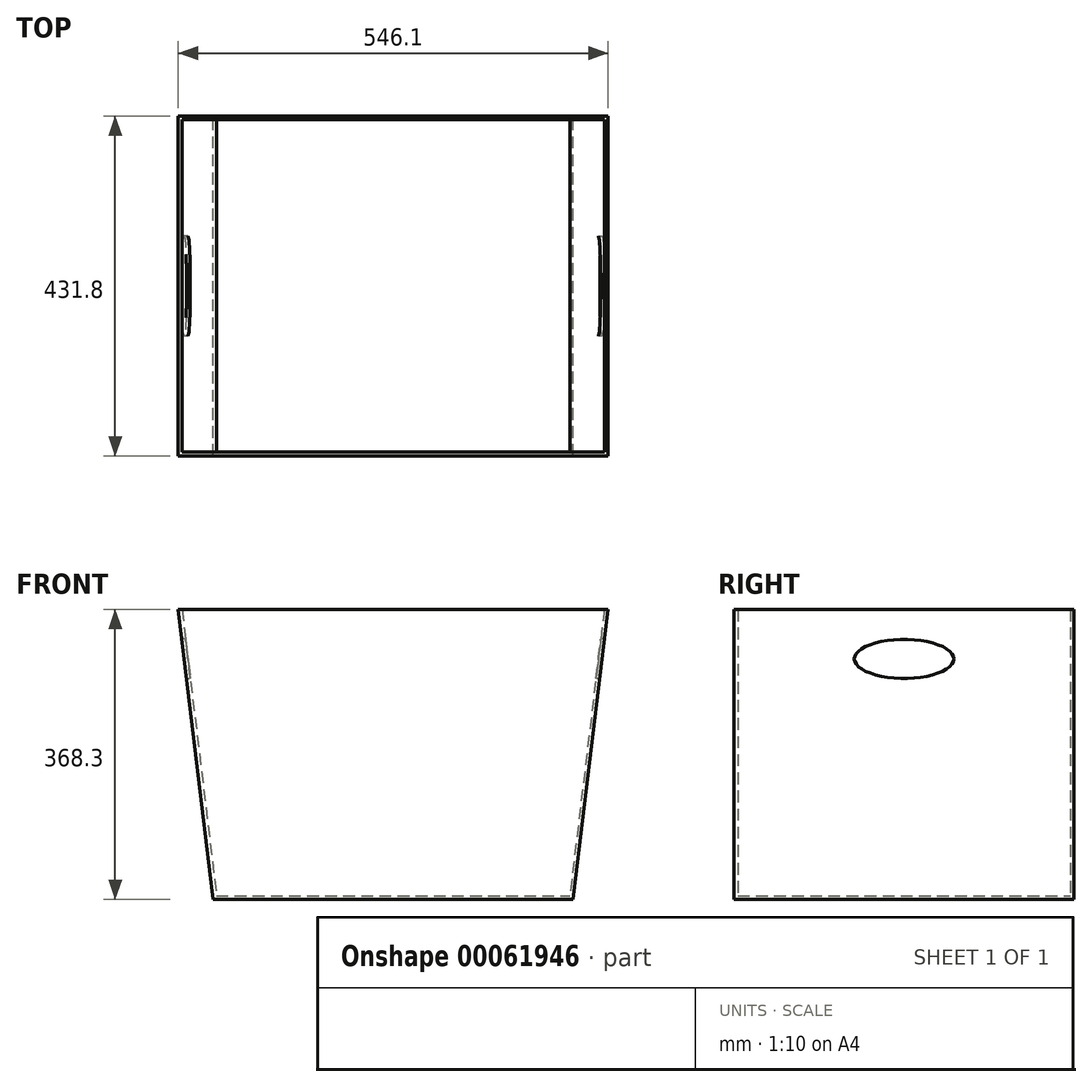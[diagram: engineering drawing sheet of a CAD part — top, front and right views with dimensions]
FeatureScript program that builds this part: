
annotation { "Feature Type Name" : "Feature", "Feature Type Description" : "" }
export const myFeature = defineFeature(function(context is Context, id is Id, definition is map)
    precondition{}
    {
        {
            var Q0;
            Q0=qCreatedBy(makeId("Front.planeOp"),FACE);
            var sketch = newSketch(context, id + "F0", { "sketchPlane" : qUnion([Q0])});
            skPoint(sketch, "E0.rect.middle", {"position": v(0, 0) * mm});
            skLineSegment(sketch, "E1", {"start": v(-273.05, 215.94) * mm, "end": v(-228.6, -152.36) * mm});
            skLineSegment(sketch, "E2", {"start": v(-228.6, -152.36) * mm, "end": v(228.6, -152.36) * mm});
            skLineSegment(sketch, "E3.MirrorCS", {"start": v(273.05, 215.94) * mm, "end": v(228.6, -152.36) * mm});
            skLineSegment(sketch, "E4", {"start": v(-273.05, 215.94) * mm, "end": v(273.05, 215.94) * mm});
            skSolve(sketch);
        }
        {
            var Q0;
            Q0=makeQuery(id+"F0.imprint","IMPRINT",FACE,{"disambiguationData":[TD([[makeQuery(id+"F0.imprint","IMPRINT",EDGE,{"derivedFrom":sQuery(id+"F0.wireOp",EDGE,"E1")}),1.0]])]});
            extrude(context, id + "F1", {"entities" : qUnion([Q0]), "depth" : 431.8 * mm});
        }
        {
            var Q0;
            Q0=makeQuery(id+"F1.opExtrude","SWEPT_FACE",FACE,{"disambiguationData":[OSD([sQuery(id+"F0.wireOp",EDGE,"E4")])]});
            shell(context, id + "F2", {"entities" : qUnion([Q0]), "thickness" : 4.76 * mm});
        }
        {
            var Q0;
            Q0=makeQuery(id+"F1.opExtrude","SWEPT_FACE",FACE,{"disambiguationData":[OSD([sQuery(id+"F0.wireOp",EDGE,"E1")])]});
            var sketch = newSketch(context, id + "F3", { "sketchPlane" : qUnion([Q0])});
            skEllipse(sketch, "E5", {"center": v(215.9, 183.6) * mm, "majorRadius": 63.5 * mm, "minorRadius": 25.4 * mm, "majorAxis": v(-1, 0)});
            skPoint(sketch, "E5.centerSnap0", {"position": v(215.9, 247.1) * mm});
            skSolve(sketch);
        }
        {
            var Q0;
            Q0=makeQuery(id+"F3.imprint","IMPRINT",FACE,{"disambiguationData":[TD([[makeQuery(id+"F3.imprint","IMPRINT",EDGE,{"derivedFrom":sQuery(id+"F3.wireOp",EDGE,"E5")}),1.0]])]});
            extrude(context, id + "F4", {"entities" : qUnion([Q0]), "operationType" : NewBodyOperationType.REMOVE, "oppositeDirection" : true, "depth" : 25.4 * mm});
        }
        {
            var Q0;
            Q0=makeQuery(id+"F1.opExtrude","SWEPT_FACE",FACE,{"disambiguationData":[OSD([sQuery(id+"F0.wireOp",EDGE,"E3.MirrorCS")])]});
            var sketch = newSketch(context, id + "F5", { "sketchPlane" : qUnion([Q0])});
            skEllipse(sketch, "E6", {"center": v(-215.9, 183.6) * mm, "majorRadius": 63.5 * mm, "minorRadius": 25.4 * mm, "majorAxis": v(1, 0)});
            skPoint(sketch, "E6.centerSnap0", {"position": v(-215.9, 247.1) * mm});
            skSolve(sketch);
        }
        {
            var Q0;
            Q0=makeQuery(id+"F5.imprint","IMPRINT",FACE,{"disambiguationData":[TD([[makeQuery(id+"F5.imprint","IMPRINT",EDGE,{"derivedFrom":sQuery(id+"F5.wireOp",EDGE,"E6")}),1.0]])]});
            extrude(context, id + "F6", {"entities" : qUnion([Q0]), "operationType" : NewBodyOperationType.REMOVE, "oppositeDirection" : true, "depth" : 25.4 * mm});
        }
    });
